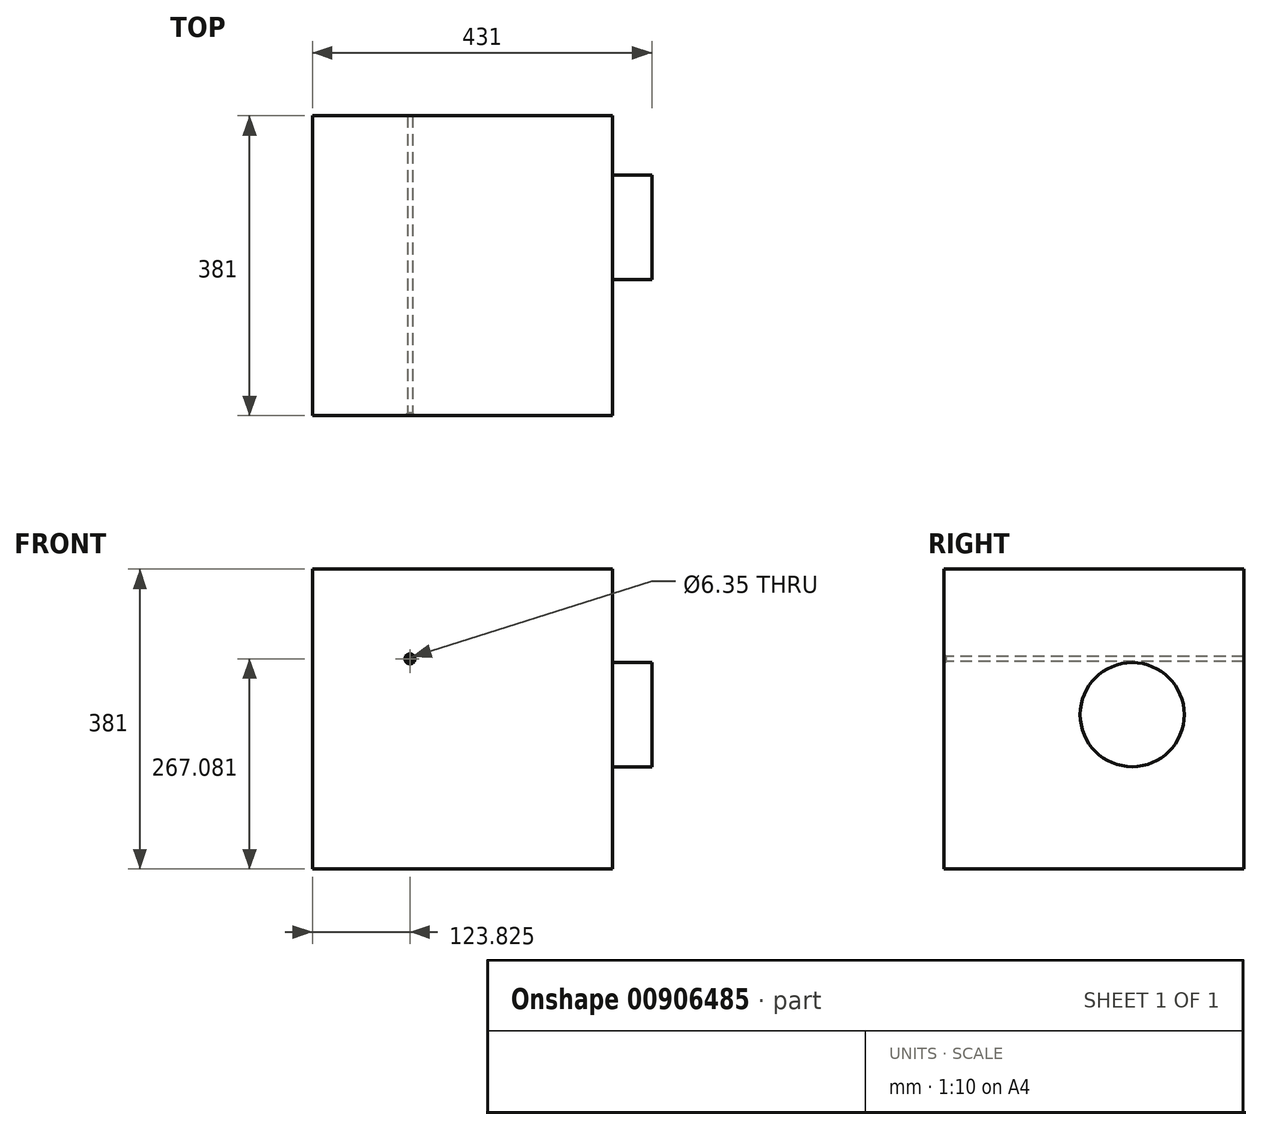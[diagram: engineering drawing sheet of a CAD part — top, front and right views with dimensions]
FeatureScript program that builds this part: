
annotation { "Feature Type Name" : "Feature", "Feature Type Description" : "" }
export const myFeature = defineFeature(function(context is Context, id is Id, definition is map)
    precondition{}
    {
        {
            var Q0;
            Q0=qCreatedBy(makeId("Front.planeOp"),FACE);
            var sketch = newSketch(context, id + "F0", { "sketchPlane" : qUnion([Q0])});
            skLineSegment(sketch, "E0.bottom", {"start": v(0, 0) * mm, "end": v(381, 0) * mm});
            skLineSegment(sketch, "E0.top", {"start": v(0, 381) * mm, "end": v(381, 381) * mm});
            skLineSegment(sketch, "E0.left", {"start": v(0, 0) * mm, "end": v(0, 381) * mm});
            skLineSegment(sketch, "E0.right", {"start": v(381, 0) * mm, "end": v(381, 381) * mm});
            skSolve(sketch);
        }
        {
            var Q0;
            Q0=qSketchRegion(id+"F0",true);
            extrude(context, id + "F1", {"entities" : qUnion([Q0]), "depth" : 381 * mm, "offsetDistance" : 25.4 * mm});
        }
        {
            var Q0;
            Q0=makeQuery(id+"F1.opExtrude","CAP_FACE",FACE,{"disambiguationData":[OSD([sQuery(id+"F0.wireOp",EDGE,"E0.bottom"),sQuery(id+"F0.wireOp",EDGE,"E0.top"),sQuery(id+"F0.wireOp",EDGE,"E0.left"),sQuery(id+"F0.wireOp",EDGE,"E0.right")])],"isStart":false});
            var sketch = newSketch(context, id + "F2", { "sketchPlane" : qUnion([Q0])});
            skPoint(sketch, "E1", {"position": v(123.83, 267.08) * mm});
            skSolve(sketch);
        }
        {
            var Q0;
            Q0=sQuery(id+"F2.wireOp",VERTEX,"E1");
            var Q1;
            Q1=makeQuery(id+"F1.opExtrude","SWEPT_BODY",BODY,{"disambiguationData":[OSD([sQuery(id+"F0.wireOp",EDGE,"E0.bottom"),sQuery(id+"F0.wireOp",EDGE,"E0.top"),sQuery(id+"F0.wireOp",EDGE,"E0.left"),sQuery(id+"F0.wireOp",EDGE,"E0.right")])]});
            hole(context, id + "F3", {"style" : HoleStyle.C_SINK, "endStyle" : HoleEndStyle.THROUGH, "holeDiameter" : 6.35 * mm, "cSinkDiameter" : 12.7 * mm, "cSinkAngle" : 90 * degree, "majorDiameter" : 6.35 * mm, "isTappedThrough" : true, "tappedDepth" : 12.7 * mm, "tapClearance" : 3, "locations" : qUnion([Q0]), "scope" : qUnion([Q1])});
        }
        {
            var Q0;
            Q0=makeQuery(id+"F1.opExtrude","SWEPT_FACE",FACE,{"disambiguationData":[OSD([sQuery(id+"F0.wireOp",EDGE,"E0.right")])]});
            var sketch = newSketch(context, id + "F4", { "sketchPlane" : qUnion([Q0])});
            skCircle(sketch, "E2", {"center": v(-141.75, 196.2) * mm, "radius": 66.12 * mm});
            skSolve(sketch);
        }
        {
            var Q0;
            Q0 = qSketchRegion(id + "F4", true);
            extrude(context, id + "F5", {"entities" : qUnion([Q0]), "operationType" : NewBodyOperationType.ADD, "depth" : 50 * mm, "offsetDistance" : 25 * mm});
        }
    });
